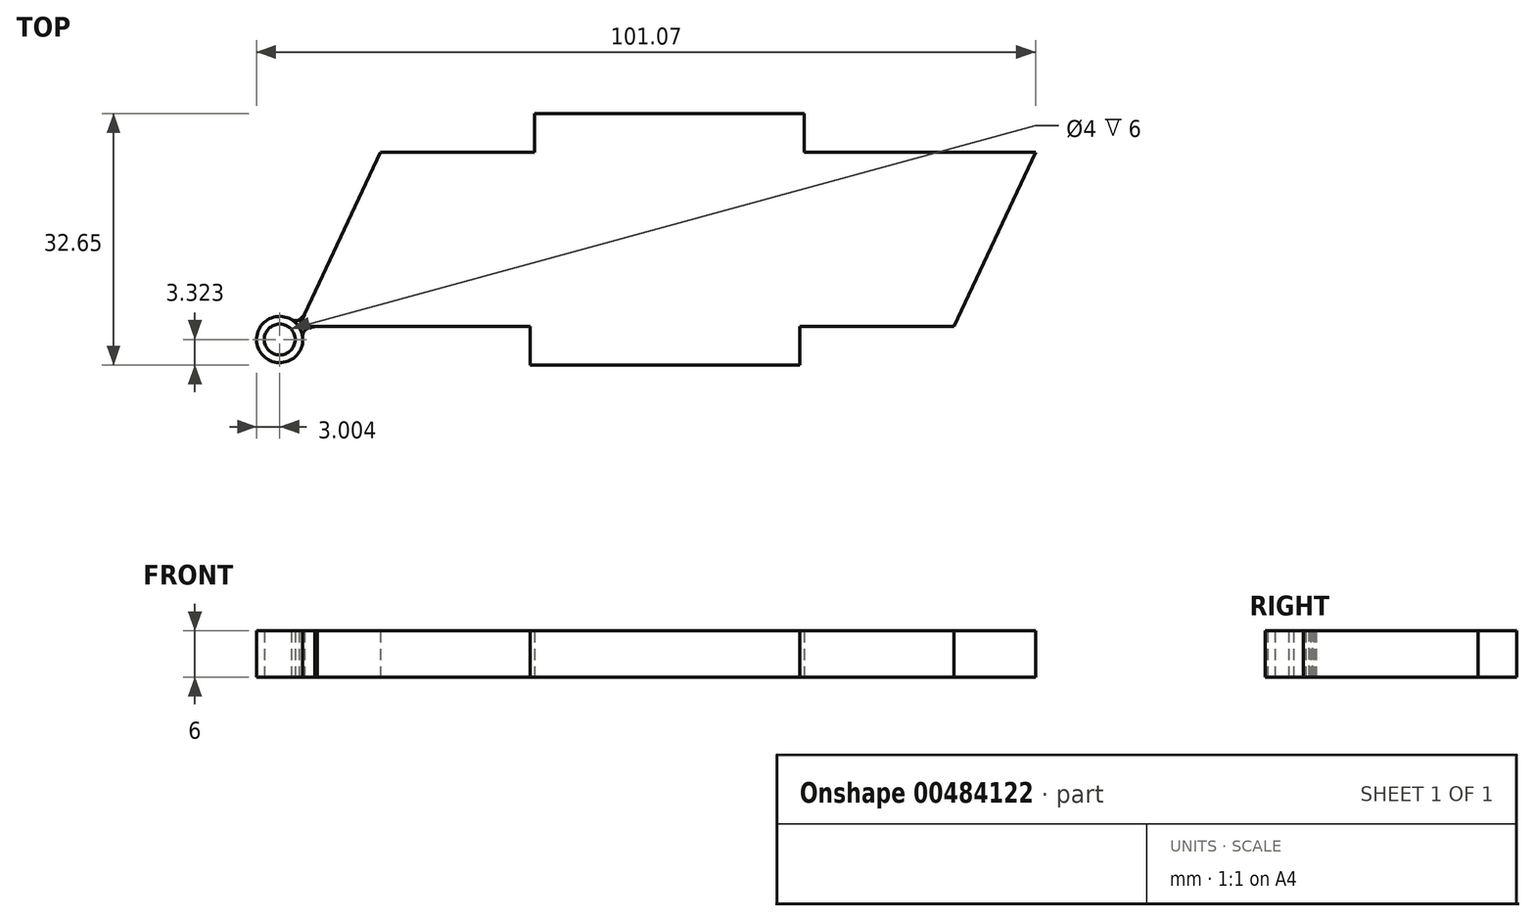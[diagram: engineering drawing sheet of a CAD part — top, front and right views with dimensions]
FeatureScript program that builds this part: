
annotation { "Feature Type Name" : "Feature", "Feature Type Description" : "" }
export const myFeature = defineFeature(function(context is Context, id is Id, definition is map)
    precondition{}
    {
        {
            var Q0;
            Q0=qCreatedBy(makeId("Top.planeOp"),FACE);
            var sketch = newSketch(context, id + "F0", { "sketchPlane" : qUnion([Q0])});
            skLineSegment(sketch, "E0", {"start": v(-50.59, 28.33) * mm, "end": v(-40.01, 50.98) * mm});
            skLineSegment(sketch, "E1", {"start": v(-40.01, 50.98) * mm, "end": v(-20.01, 50.98) * mm});
            skLineSegment(sketch, "E2", {"start": v(-20.01, 50.98) * mm, "end": v(-20.01, 55.98) * mm});
            skLineSegment(sketch, "E3", {"start": v(-20.01, 55.98) * mm, "end": v(14.99, 55.98) * mm});
            skLineSegment(sketch, "E4", {"start": v(14.99, 55.98) * mm, "end": v(14.99, 50.98) * mm});
            skLineSegment(sketch, "E5", {"start": v(14.99, 50.98) * mm, "end": v(44.99, 50.98) * mm});
            skLineSegment(sketch, "E6", {"start": v(44.99, 50.98) * mm, "end": v(34.41, 28.33) * mm});
            skLineSegment(sketch, "E7", {"start": v(34.41, 28.33) * mm, "end": v(14.41, 28.33) * mm});
            skLineSegment(sketch, "E8", {"start": v(14.41, 28.33) * mm, "end": v(14.41, 23.33) * mm});
            skLineSegment(sketch, "E9", {"start": v(14.41, 23.33) * mm, "end": v(-20.59, 23.33) * mm});
            skLineSegment(sketch, "E10", {"start": v(-20.59, 23.33) * mm, "end": v(-20.59, 28.33) * mm});
            skLineSegment(sketch, "E11", {"start": v(-20.59, 28.33) * mm, "end": v(-50.59, 28.33) * mm});
            skCircle(sketch, "E12", {"center": v(-53.08, 26.65) * mm, "radius": 3 * mm});
            skFitSpline(sketch, "E13", {"points": [v(-51.6, 29.26) * mm, v(-50.65, 29.15) * mm, v(-49.84, 29.94) * mm, v(-49.86, 29.88) * mm, v(-50.02, 29.53) * mm], "startDerivative": vector(2.44, -0.83) * mm, "endDerivative": vector(-0.81, -1.8) * mm});
            skFitSpline(sketch, "E14", {"points": [v(-50.08, 26.42) * mm, v(-49.88, 27.78) * mm, v(-48.5, 28.33) * mm, v(-48.18, 28.33) * mm, v(-48.15, 28.33) * mm], "startDerivative": vector(-0.07, 3.54) * mm, "endDerivative": vector(0.37, 0.02) * mm});
            skCircle(sketch, "E15", {"center": v(-53.08, 26.65) * mm, "radius": 2 * mm});
            skSolve(sketch);
        }
        {
            var Q0;
            {var subQ6=sQuery(id+"F0.wireOp",EDGE,"E1");Q0=makeQuery(id+"F0.imprint","IMPRINT",FACE,{"disambiguationData":[TD([[makeQuery(id+"F0.imprint","IMPRINT",EDGE,{"derivedFrom":subQ6}),-1.0]])]});}
            var Q1;
            Q1=makeQuery(id+"F0.imprint","IMPRINT",FACE,{"disambiguationData":[TD([[makeQuery(id+"F0.imprint","IMPRINT",EDGE,{"derivedFrom":sQuery(id+"F0.wireOp",EDGE,"E15")}),-1.0]])]});
            extrude(context, id + "F1", {"entities" : qUnion([Q0, Q1]), "depth" : 6 * mm});
        }
        {
            var Q0;
            {var subQ0=sQuery(id+"F0.wireOp",EDGE,"E13");var subQ3=sQuery(id+"F0.wireOp",EDGE,"E0");var subQ4=makeQuery(id+"F0.imprint","INTERSECT",VERTEX,{"disambiguationData":[OD(1.0)],"derivedFrom":[subQ3,subQ0]});Q0=makeQuery(id+"F0.imprint","IMPRINT",FACE,{"disambiguationData":[TD([[makeQuery(id+"F0.imprint","IMPRINT",EDGE,{"disambiguationData":[TD([[subQ4,1.0]])],"derivedFrom":subQ3}),1.0]])]});}
            var Q1;
            {var subQ1=sQuery(id+"F0.wireOp",EDGE,"E11");var subQ3=sQuery(id+"F0.wireOp",EDGE,"E14");var subQ4=makeQuery(id+"F0.imprint","INTERSECT",VERTEX,{"disambiguationData":[OD(2.0)],"derivedFrom":[subQ1,subQ3]});Q1=makeQuery(id+"F0.imprint","IMPRINT",FACE,{"disambiguationData":[TD([[makeQuery(id+"F0.imprint","IMPRINT",EDGE,{"disambiguationData":[TD([[subQ4,1.0]])],"derivedFrom":subQ3}),1.0]])]});}
            extrude(context, id + "F2", {"entities" : qUnion([Q0, Q1]), "depth" : 6 * mm});
        }
    });
